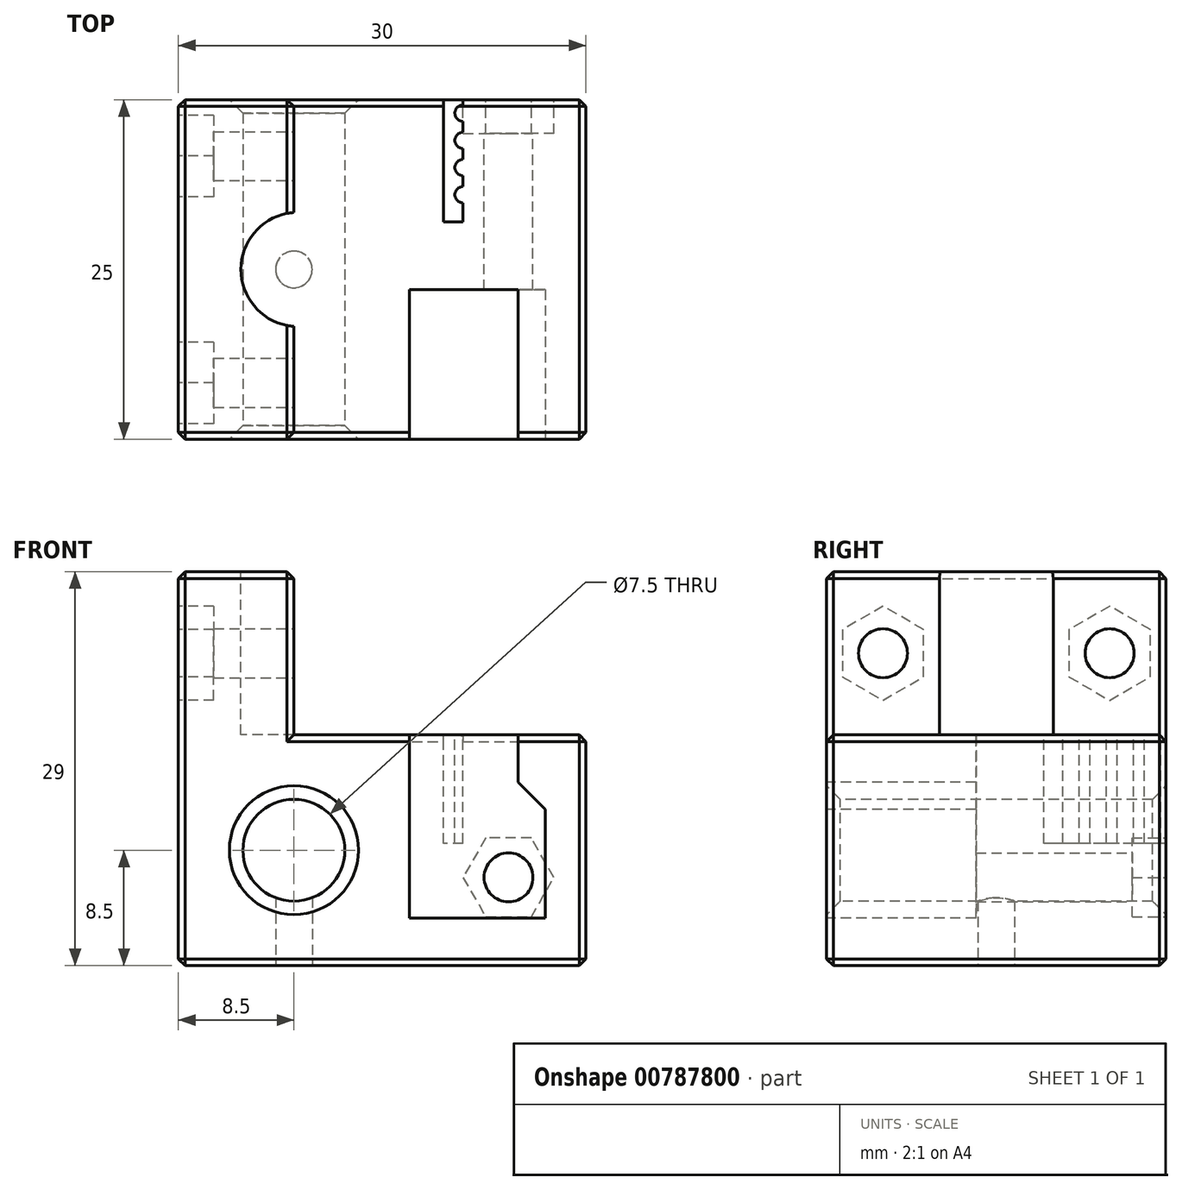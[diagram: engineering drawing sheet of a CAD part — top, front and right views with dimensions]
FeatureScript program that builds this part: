
annotation { "Feature Type Name" : "Feature", "Feature Type Description" : "" }
export const myFeature = defineFeature(function(context is Context, id is Id, definition is map)
    precondition{}
    {
        {
            var Q0;
            Q0=qCreatedBy(makeId("Top.planeOp"),FACE);
            var sketch = newSketch(context, id + "F0", { "sketchPlane" : qUnion([Q0])});
            skLineSegment(sketch, "E0.bottom", {"start": v(15, 12.5) * mm, "end": v(-15, 12.5) * mm});
            skLineSegment(sketch, "E0.top", {"start": v(15, -12.5) * mm, "end": v(-15, -12.5) * mm});
            skLineSegment(sketch, "E0.left", {"start": v(15, 12.5) * mm, "end": v(15, -12.5) * mm});
            skLineSegment(sketch, "E0.right", {"start": v(-15, 12.5) * mm, "end": v(-15, -12.5) * mm});
            skPoint(sketch, "E0.middle", {"position": v(0, 0) * mm});
            skSolve(sketch);
        }
        {
            var Q0;
            Q0=makeQuery(id+"F0.imprint","IMPRINT",FACE,{"disambiguationData":[TD([[makeQuery(id+"F0.imprint","IMPRINT",EDGE,{"derivedFrom":sQuery(id+"F0.wireOp",EDGE,"E0.bottom")}),1.0]])]});
            extrude(context, id + "F1", {"entities" : qUnion([Q0]), "depth" : 17 * mm, "offsetDistance" : 25 * mm});
        }
        {
            var Q0;
            Q0=makeQuery(id+"F1.opExtrude","SWEPT_FACE",FACE,{"disambiguationData":[OSD([sQuery(id+"F0.wireOp",EDGE,"E0.top")])]});
            var sketch = newSketch(context, id + "F2", { "sketchPlane" : qUnion([Q0])});
            skLineSegment(sketch, "E1", {"start": v(2, 17) * mm, "end": v(10, 17) * mm});
            skLineSegment(sketch, "E2", {"start": v(10, 17) * mm, "end": v(10, 13.5) * mm});
            skLineSegment(sketch, "E3", {"start": v(10, 13.5) * mm, "end": v(12, 11.5) * mm});
            skLineSegment(sketch, "E4", {"start": v(12, 11.5) * mm, "end": v(12, 3.5) * mm});
            skLineSegment(sketch, "E5", {"start": v(12, 3.5) * mm, "end": v(2, 3.5) * mm});
            skLineSegment(sketch, "E6", {"start": v(2, 3.5) * mm, "end": v(2, 17) * mm});
            skSolve(sketch);
        }
        {
            var Q0;
            Q0=makeQuery(id+"F2.imprint","IMPRINT",FACE,{"disambiguationData":[TD([[makeQuery(id+"F2.imprint","IMPRINT",EDGE,{"derivedFrom":sQuery(id+"F2.wireOp",EDGE,"E1")}),1.0]])]});
            extrude(context, id + "F3", {"entities" : qUnion([Q0]), "operationType" : NewBodyOperationType.REMOVE, "oppositeDirection" : true, "depth" : 11 * mm, "offsetDistance" : 25 * mm});
        }
        {
            var Q0;
            Q0=makeQuery(id+"F1.opExtrude","SWEPT_FACE",FACE,{"disambiguationData":[OSD([sQuery(id+"F0.wireOp",EDGE,"E0.top")])]});
            var sketch = newSketch(context, id + "F4", { "sketchPlane" : qUnion([Q0])});
            skCircle(sketch, "E7", {"center": v(-6.5, 8.5) * mm, "radius": 3.75 * mm});
            skPoint(sketch, "E7.centerSnap0", {"position": v(-6.5, 17) * mm});
            skPoint(sketch, "E7.centerSnap1", {"position": v(-15, 8.5) * mm});
            skSolve(sketch);
        }
        {
            var Q0;
            Q0=makeQuery(id+"F4.imprint","IMPRINT",FACE,{"disambiguationData":[TD([[makeQuery(id+"F4.imprint","IMPRINT",EDGE,{"derivedFrom":sQuery(id+"F4.wireOp",EDGE,"E7")}),1.0]])]});
            extrude(context, id + "F5", {"entities" : qUnion([Q0]), "operationType" : NewBodyOperationType.REMOVE, "endBound" : BoundingType.UP_TO_NEXT, "oppositeDirection" : true, "depth" : 25 * mm, "offsetDistance" : 25 * mm});
        }
        {
            var Q0;
            Q0=makeQuery(id+"F1.opExtrude","CAP_FACE",FACE,{"disambiguationData":[OSD([sQuery(id+"F0.wireOp",EDGE,"E0.bottom"),sQuery(id+"F0.wireOp",EDGE,"E0.top"),sQuery(id+"F0.wireOp",EDGE,"E0.left"),sQuery(id+"F0.wireOp",EDGE,"E0.right")])],"isStart":false});
            var sketch = newSketch(context, id + "F6", { "sketchPlane" : qUnion([Q0])});
            skLineSegment(sketch, "E8.bottom", {"start": v(-6.5, -12.5) * mm, "end": v(-15, -12.5) * mm});
            skLineSegment(sketch, "E8.top", {"start": v(-6.5, 12.5) * mm, "end": v(-15, 12.5) * mm});
            skLineSegment(sketch, "E8.left", {"start": v(-6.5, -12.5) * mm, "end": v(-6.5, 12.5) * mm});
            skLineSegment(sketch, "E8.right", {"start": v(-15, -12.5) * mm, "end": v(-15, 12.5) * mm});
            skSolve(sketch);
        }
        {
            var Q0;
            {var subQ1=sQuery(id+"F6.wireOp",EDGE,"E8.bottom");Q0=makeQuery(id+"F6.imprint","IMPRINT",FACE,{"disambiguationData":[TD([[makeQuery(id+"F6.imprint","IMPRINT",EDGE,{"derivedFrom":subQ1}),-1.0]])]});}
            extrude(context, id + "F7", {"entities" : qUnion([Q0]), "operationType" : NewBodyOperationType.ADD, "depth" : 12 * mm, "offsetDistance" : 25 * mm});
        }
        {
            var Q0;
            Q0=makeQuery(id+"F7.opExtrude","CAP_FACE",FACE,{"disambiguationData":[OSD([sQuery(id+"F6.wireOp",EDGE,"E8.bottom"),sQuery(id+"F6.wireOp",EDGE,"E8.top"),sQuery(id+"F6.wireOp",EDGE,"E8.left"),sQuery(id+"F6.wireOp",EDGE,"E8.right")])],"isStart":false});
            var sketch = newSketch(context, id + "F8", { "sketchPlane" : qUnion([Q0])});
            skArc(sketch, "E9", {"start": v(-6.5, 4.19) * mm, "mid": v(-10.4, 0) * mm, "end": v(-6.5, -4.19) * mm});
            skLineSegment(sketch, "E10", {"start": v(-6.5, -4.19) * mm, "end": v(-6.5, 4.19) * mm});
            skSolve(sketch);
        }
        {
            var Q0;
            Q0=makeQuery(id+"F8.imprint","IMPRINT",FACE,{"disambiguationData":[TD([[makeQuery(id+"F8.imprint","IMPRINT",EDGE,{"derivedFrom":sQuery(id+"F8.wireOp",EDGE,"E9")}),1.0]])]});
            extrude(context, id + "F9", {"entities" : qUnion([Q0]), "operationType" : NewBodyOperationType.REMOVE, "oppositeDirection" : true, "depth" : 12 * mm, "offsetDistance" : 25 * mm});
        }
        {
            var Q0;
            {var subQ0=sQuery(id+"F6.wireOp",EDGE,"E8.left");var subQ2=sQuery(id+"F0.wireOp",EDGE,"E0.bottom");Q0=makeQuery(id+"F9.boolean.opBoolean","SPLIT",FACE,{"disambiguationData":[TD([makeQuery(id+"F1.opExtrude","SWEPT_FACE",FACE,{"disambiguationData":[OSD([subQ2])]})])],"derivedFrom":makeQuery(id+"F7.opExtrude","SWEPT_FACE",FACE,{"disambiguationData":[OSD([subQ0])]})});}
            var sketch = newSketch(context, id + "F10", { "sketchPlane" : qUnion([Q0])});
            skPoint(sketch, "E11.centerSnap0", {"position": v(-12.5, 14.5) * mm});
            skPoint(sketch, "E11.centerSnap1", {"position": v(0, 29) * mm});
            skCircle(sketch, "E12", {"center": v(8.34, 23) * mm, "radius": 1.8 * mm});
            skPoint(sketch, "E12.centerSnap0", {"position": v(12.5, 23) * mm});
            skPoint(sketch, "E12.centerSnap1", {"position": v(8.34, 29) * mm});
            skPoint(sketch, "E13.0", {"position": v(-8.34, 29) * mm});
            skCircle(sketch, "E14", {"center": v(-8.34, 23) * mm, "radius": 1.8 * mm});
            skPoint(sketch, "E14.centerSnap0", {"position": v(4.19, 23) * mm});
            skSolve(sketch);
        }
        {
            var Q0;
            Q0=makeQuery(id+"F10.imprint","IMPRINT",FACE,{"disambiguationData":[TD([[makeQuery(id+"F10.imprint","IMPRINT",EDGE,{"derivedFrom":sQuery(id+"F10.wireOp",EDGE,"E14")}),1.0]])]});
            var Q1;
            Q1=makeQuery(id+"F10.imprint","IMPRINT",FACE,{"disambiguationData":[TD([[makeQuery(id+"F10.imprint","IMPRINT",EDGE,{"derivedFrom":sQuery(id+"F10.wireOp",EDGE,"E12")}),1.0]])]});
            extrude(context, id + "F11", {"entities" : qUnion([Q0, Q1]), "operationType" : NewBodyOperationType.REMOVE, "endBound" : BoundingType.UP_TO_NEXT, "oppositeDirection" : true, "depth" : 25 * mm, "offsetDistance" : 25 * mm});
        }
        {
            var Q0;
            Q0=makeQuery(id+"F7.boolean.opBoolean","MERGE",FACE,{"derivedFrom":[makeQuery(id+"F1.opExtrude","SWEPT_FACE",FACE,{"disambiguationData":[OSD([sQuery(id+"F0.wireOp",EDGE,"E0.right")])]}),makeQuery(id+"F7.opExtrude","SWEPT_FACE",FACE,{"disambiguationData":[OSD([sQuery(id+"F6.wireOp",EDGE,"E8.right")])]})]});
            var sketch = newSketch(context, id + "F12", { "sketchPlane" : qUnion([Q0])});
            skCircle(sketch, "E15.cCircle", {"center": v(8.34, 23) * mm, "radius": 3 * mm, "construction": true});
            skLineSegment(sketch, "E15.0", {"start": v(11.34, 24.73) * mm, "end": v(11.34, 21.27) * mm});
            skLineSegment(sketch, "E15.1", {"start": v(11.34, 21.27) * mm, "end": v(8.34, 19.54) * mm});
            skLineSegment(sketch, "E15.2", {"start": v(8.34, 19.54) * mm, "end": v(5.34, 21.27) * mm});
            skLineSegment(sketch, "E15.3", {"start": v(5.34, 21.27) * mm, "end": v(5.34, 24.73) * mm});
            skLineSegment(sketch, "E15.4", {"start": v(5.34, 24.73) * mm, "end": v(8.34, 26.46) * mm});
            skLineSegment(sketch, "E15.5", {"start": v(8.34, 26.46) * mm, "end": v(11.34, 24.73) * mm});
            skPoint(sketch, "E15.0.midPoint", {"position": v(11.34, 23) * mm});
            skCircle(sketch, "E16.cCircle", {"center": v(-8.34, 23) * mm, "radius": 3 * mm, "construction": true});
            skLineSegment(sketch, "E16.0", {"start": v(-5.34, 24.73) * mm, "end": v(-5.34, 21.27) * mm});
            skLineSegment(sketch, "E16.1", {"start": v(-5.34, 21.27) * mm, "end": v(-8.34, 19.54) * mm});
            skLineSegment(sketch, "E16.2", {"start": v(-8.34, 19.54) * mm, "end": v(-11.34, 21.27) * mm});
            skLineSegment(sketch, "E16.3", {"start": v(-11.34, 21.27) * mm, "end": v(-11.34, 24.73) * mm});
            skLineSegment(sketch, "E16.4", {"start": v(-11.34, 24.73) * mm, "end": v(-8.34, 26.46) * mm});
            skLineSegment(sketch, "E16.5", {"start": v(-8.34, 26.46) * mm, "end": v(-5.34, 24.73) * mm});
            skPoint(sketch, "E16.0.midPoint", {"position": v(-5.34, 23) * mm});
            skSolve(sketch);
        }
        {
            var Q0;
            Q0=makeQuery(id+"F12.imprint","IMPRINT",FACE,{"disambiguationData":[TD([[makeQuery(id+"F12.imprint","IMPRINT",EDGE,{"derivedFrom":sQuery(id+"F12.wireOp",EDGE,"E15.0")}),-1.0]])]});
            var Q1;
            Q1=makeQuery(id+"F12.imprint","IMPRINT",FACE,{"disambiguationData":[TD([[makeQuery(id+"F12.imprint","IMPRINT",EDGE,{"derivedFrom":sQuery(id+"F12.wireOp",EDGE,"E16.0")}),-1.0]])]});
            extrude(context, id + "F13", {"entities" : qUnion([Q0, Q1]), "operationType" : NewBodyOperationType.REMOVE, "oppositeDirection" : true, "depth" : 2.6 * mm, "offsetDistance" : 25 * mm});
        }
        {
            var Q0;
            {var subQ0=sQuery(id+"F0.wireOp",EDGE,"E0.left");var subQ1=sQuery(id+"F0.wireOp",EDGE,"E0.top");var subQ4=sQuery(id+"F0.wireOp",EDGE,"E0.bottom");Q0=makeQuery(id+"F7.boolean.opBoolean","SPLIT",FACE,{"disambiguationData":[TD([makeQuery(id+"F1.opExtrude","SWEPT_FACE",FACE,{"disambiguationData":[OSD([subQ0])]})])],"derivedFrom":makeQuery(id+"F1.opExtrude","CAP_FACE",FACE,{"disambiguationData":[OSD([subQ4,subQ1,subQ0,sQuery(id+"F0.wireOp",EDGE,"E0.right")])],"isStart":false})});}
            var sketch = newSketch(context, id + "F14", { "sketchPlane" : qUnion([Q0])});
            skLineSegment(sketch, "E17.bottom", {"start": v(4.5, 12.5) * mm, "end": v(5.95, 12.5) * mm});
            skLineSegment(sketch, "E17.top", {"start": v(4.5, 3.5) * mm, "end": v(5.95, 3.5) * mm});
            skLineSegment(sketch, "E17.left", {"start": v(4.5, 12.5) * mm, "end": v(4.5, 3.5) * mm});
            skLineSegment(sketch, "E17.right", {"start": v(5.95, 12.5) * mm, "end": v(5.95, 12.1) * mm});
            skArc(sketch, "E18", {"start": v(5.95, 12.1) * mm, "mid": v(5.35, 11.5) * mm, "end": v(5.95, 10.9) * mm});
            skArc(sketch, "E19.0.1.0", {"start": v(5.95, 10.1) * mm, "mid": v(5.35, 9.5) * mm, "end": v(5.95, 8.9) * mm});
            skArc(sketch, "E19.0.2.0", {"start": v(5.95, 8.1) * mm, "mid": v(5.35, 7.5) * mm, "end": v(5.95, 6.9) * mm});
            skArc(sketch, "E19.0.3.0", {"start": v(5.95, 6.1) * mm, "mid": v(5.35, 5.5) * mm, "end": v(5.95, 4.9) * mm});
            skLineSegment(sketch, "E19.direction1", {"start": v(5.95, 11.5) * mm, "end": v(13.56, 11.5) * mm, "construction": true});
            skLineSegment(sketch, "E19.direction2", {"start": v(5.95, 11.5) * mm, "end": v(5.95, 9.5) * mm, "construction": true});
            skLineSegment(sketch, "E20.trimOffspring", {"start": v(5.95, 4.9) * mm, "end": v(5.95, 3.5) * mm});
            skLineSegment(sketch, "E21.trimOffspring", {"start": v(5.95, 6.9) * mm, "end": v(5.95, 6.1) * mm});
            skLineSegment(sketch, "E22.trimOffspring", {"start": v(5.95, 8.9) * mm, "end": v(5.95, 8.1) * mm});
            skLineSegment(sketch, "E23.trimOffspring", {"start": v(5.95, 11.5) * mm, "end": v(5.95, 9.5) * mm});
            skSolve(sketch);
        }
        {
            var Q0;
            Q0=makeQuery(id+"F14.imprint","IMPRINT",FACE,{"disambiguationData":[TD([[makeQuery(id+"F14.imprint","IMPRINT",EDGE,{"derivedFrom":sQuery(id+"F14.wireOp",EDGE,"E17.bottom")}),1.0]])]});
            extrude(context, id + "F15", {"entities" : qUnion([Q0]), "operationType" : NewBodyOperationType.REMOVE, "oppositeDirection" : true, "depth" : 8 * mm, "offsetDistance" : 25 * mm});
        }
        {
            var Q0;
            Q0=makeQuery(id+"F7.boolean.opBoolean","MERGE",FACE,{"derivedFrom":[makeQuery(id+"F1.opExtrude","SWEPT_FACE",FACE,{"disambiguationData":[OSD([sQuery(id+"F0.wireOp",EDGE,"E0.bottom")])]}),makeQuery(id+"F7.opExtrude","SWEPT_FACE",FACE,{"disambiguationData":[OSD([sQuery(id+"F6.wireOp",EDGE,"E8.top")])]})]});
            var sketch = newSketch(context, id + "F16", { "sketchPlane" : qUnion([Q0])});
            skCircle(sketch, "E24", {"center": v(-9.3, 6.5) * mm, "radius": 1.8 * mm});
            skSolve(sketch);
        }
        {
            var Q0;
            Q0=makeQuery(id+"F16.imprint","IMPRINT",FACE,{"disambiguationData":[TD([[makeQuery(id+"F16.imprint","IMPRINT",EDGE,{"derivedFrom":sQuery(id+"F16.wireOp",EDGE,"E24")}),1.0]])]});
            extrude(context, id + "F17", {"entities" : qUnion([Q0]), "operationType" : NewBodyOperationType.REMOVE, "endBound" : BoundingType.UP_TO_NEXT, "oppositeDirection" : true, "depth" : 25 * mm, "offsetDistance" : 25 * mm});
        }
        {
            var Q0;
            Q0=makeQuery(id+"F7.boolean.opBoolean","MERGE",FACE,{"derivedFrom":[makeQuery(id+"F1.opExtrude","SWEPT_FACE",FACE,{"disambiguationData":[OSD([sQuery(id+"F0.wireOp",EDGE,"E0.bottom")])]}),makeQuery(id+"F7.opExtrude","SWEPT_FACE",FACE,{"disambiguationData":[OSD([sQuery(id+"F6.wireOp",EDGE,"E8.top")])]})]});
            var sketch = newSketch(context, id + "F18", { "sketchPlane" : qUnion([Q0])});
            skCircle(sketch, "E25.cCircle", {"center": v(-9.3, 6.5) * mm, "radius": 2.9 * mm, "construction": true});
            skLineSegment(sketch, "E25.0", {"start": v(-10.97, 9.4) * mm, "end": v(-7.63, 9.4) * mm});
            skLineSegment(sketch, "E25.1", {"start": v(-7.63, 9.4) * mm, "end": v(-5.95, 6.5) * mm});
            skLineSegment(sketch, "E25.2", {"start": v(-5.95, 6.5) * mm, "end": v(-7.63, 3.6) * mm});
            skLineSegment(sketch, "E25.3", {"start": v(-7.63, 3.6) * mm, "end": v(-10.97, 3.6) * mm});
            skLineSegment(sketch, "E25.4", {"start": v(-10.97, 3.6) * mm, "end": v(-12.65, 6.5) * mm});
            skLineSegment(sketch, "E25.5", {"start": v(-12.65, 6.5) * mm, "end": v(-10.97, 9.4) * mm});
            skPoint(sketch, "E25.0.midPoint", {"position": v(-9.3, 9.4) * mm});
            skSolve(sketch);
        }
        {
            var Q0;
            Q0=makeQuery(id+"F18.imprint","IMPRINT",FACE,{"disambiguationData":[TD([[makeQuery(id+"F18.imprint","IMPRINT",EDGE,{"derivedFrom":sQuery(id+"F18.wireOp",EDGE,"E25.0")}),-1.0]])]});
            extrude(context, id + "F19", {"entities" : qUnion([Q0]), "operationType" : NewBodyOperationType.REMOVE, "oppositeDirection" : true, "depth" : 2.5 * mm, "offsetDistance" : 25 * mm});
        }
        {
            var Q0;
            Q0=makeQuery(id+"F7.boolean.opBoolean","MERGE",FACE,{"derivedFrom":[makeQuery(id+"F1.opExtrude","SWEPT_FACE",FACE,{"disambiguationData":[OSD([sQuery(id+"F0.wireOp",EDGE,"E0.bottom")])]}),makeQuery(id+"F7.opExtrude","SWEPT_FACE",FACE,{"disambiguationData":[OSD([sQuery(id+"F6.wireOp",EDGE,"E8.top")])]})]});
            var sketch = newSketch(context, id + "F20", { "sketchPlane" : qUnion([Q0])});
            skCircle(sketch, "E26.0", {"center": v(6.5, 8.5) * mm, "radius": 3.75 * mm});
            skCircle(sketch, "E27", {"center": v(6.5, 8.5) * mm, "radius": 3.5 * mm});
            skLineSegment(sketch, "E28", {"start": v(5.35, 11.8) * mm, "end": v(5.29, 12.05) * mm});
            skLineSegment(sketch, "E29", {"start": v(7.65, 11.8) * mm, "end": v(7.71, 12.05) * mm});
            skLineSegment(sketch, "E30", {"start": v(6.5, -1.55) * mm, "end": v(6.5, 19.4) * mm});
            skLineSegment(sketch, "E31.1.0", {"start": v(8.79, 11.15) * mm, "end": v(8.97, 11.33) * mm});
            skLineSegment(sketch, "E31.1.1", {"start": v(9.94, 9.16) * mm, "end": v(10.18, 9.22) * mm});
            skLineSegment(sketch, "E31.2.0", {"start": v(9.94, 7.84) * mm, "end": v(10.18, 7.78) * mm});
            skLineSegment(sketch, "E31.2.1", {"start": v(8.79, 5.85) * mm, "end": v(8.97, 5.67) * mm});
            skLineSegment(sketch, "E31.3.0", {"start": v(7.65, 5.2) * mm, "end": v(7.71, 4.95) * mm});
            skLineSegment(sketch, "E31.3.1", {"start": v(5.35, 5.2) * mm, "end": v(5.29, 4.95) * mm});
            skLineSegment(sketch, "E31.4.0", {"start": v(4.21, 5.85) * mm, "end": v(4.03, 5.67) * mm});
            skLineSegment(sketch, "E31.4.1", {"start": v(3.06, 7.84) * mm, "end": v(2.82, 7.78) * mm});
            skLineSegment(sketch, "E31.5.0", {"start": v(3.06, 9.16) * mm, "end": v(2.82, 9.22) * mm});
            skLineSegment(sketch, "E31.5.1", {"start": v(4.21, 11.15) * mm, "end": v(4.03, 11.33) * mm});
            skLineSegment(sketch, "E31.anchor1", {"start": v(6.5, 8.5) * mm, "end": v(5.35, 11.8) * mm, "construction": true});
            skLineSegment(sketch, "E31.anchor2", {"start": v(6.5, 8.5) * mm, "end": v(5.35, 11.8) * mm, "construction": true});
            skSolve(sketch);
        }
        {
            var Q0;
            Q0=makeQuery(id+"F1.opExtrude","CAP_EDGE",EDGE,{"disambiguationData":[OSD([sQuery(id+"F0.wireOp",EDGE,"E0.top")])],"isStart":true});
            var Q1;
            Q1=makeQuery(id+"F1.opExtrude","CAP_EDGE",EDGE,{"disambiguationData":[OSD([sQuery(id+"F0.wireOp",EDGE,"E0.right")])],"isStart":true});
            var Q2;
            Q2=makeQuery(id+"F1.opExtrude","CAP_EDGE",EDGE,{"disambiguationData":[OSD([sQuery(id+"F0.wireOp",EDGE,"E0.bottom")])],"isStart":true});
            var Q3;
            Q3=makeQuery(id+"F1.opExtrude","CAP_EDGE",EDGE,{"disambiguationData":[OSD([sQuery(id+"F0.wireOp",EDGE,"E0.left")])],"isStart":true});
            var Q4;
            Q4=makeQuery(id+"F1.opExtrude","CAP_EDGE",EDGE,{"disambiguationData":[OSD([sQuery(id+"F0.wireOp",EDGE,"E0.right")])],"isStart":false});
            var Q5;
            {var subQ0=sQuery(id+"F0.wireOp",EDGE,"E0.right");var subQ1=sQuery(id+"F0.wireOp",EDGE,"E0.bottom");Q5=makeQuery(id+"F7.boolean.opBoolean","SPLIT",EDGE,{"disambiguationData":[TD([makeQuery(id+"F1.opExtrude","SWEPT_FACE",FACE,{"disambiguationData":[OSD([subQ0])]})])],"derivedFrom":makeQuery(id+"F1.opExtrude","CAP_EDGE",EDGE,{"disambiguationData":[OSD([subQ1])],"isStart":false})});}
            var Q6;
            Q6=makeQuery(id+"F1.opExtrude","SWEPT_EDGE",EDGE,{"disambiguationData":[OSD([sQuery(id+"F0.wireOp",EDGE,"E0.bottom"),sQuery(id+"F0.wireOp",EDGE,"E0.right")])]});
            var Q7;
            Q7=makeQuery(id+"F1.opExtrude","SWEPT_EDGE",EDGE,{"disambiguationData":[OSD([sQuery(id+"F0.wireOp",EDGE,"E0.top"),sQuery(id+"F0.wireOp",EDGE,"E0.right")])]});
            var Q8;
            Q8=makeQuery(id+"F7.boolean.opBoolean","MERGE",EDGE,{"derivedFrom":[makeQuery(id+"F3.boolean.opBoolean","COPY",EDGE,{"derivedFrom":makeQuery(id+"F3.opExtrude","CAP_EDGE",EDGE,{"disambiguationData":[OSD([sQuery(id+"F2.wireOp",EDGE,"E6")])],"isStart":true})}),makeQuery(id+"F7.opExtrude","SWEPT_EDGE",EDGE,{"disambiguationData":[OSD([sQuery(id+"F6.wireOp",EDGE,"E8.bottom"),sQuery(id+"F6.wireOp",EDGE,"E8.left")])]})]});
            var Q9;
            Q9=makeQuery(id+"F3.boolean.opBoolean","COPY",EDGE,{"derivedFrom":makeQuery(id+"F3.opExtrude","CAP_EDGE",EDGE,{"disambiguationData":[OSD([sQuery(id+"F2.wireOp",EDGE,"E5")])],"isStart":true})});
            var Q10;
            Q10=makeQuery(id+"F3.boolean.opBoolean","COPY",EDGE,{"derivedFrom":makeQuery(id+"F3.opExtrude","CAP_EDGE",EDGE,{"disambiguationData":[OSD([sQuery(id+"F2.wireOp",EDGE,"E4")])],"isStart":true})});
            var Q11;
            Q11=makeQuery(id+"F3.boolean.opBoolean","COPY",EDGE,{"derivedFrom":makeQuery(id+"F3.opExtrude","CAP_EDGE",EDGE,{"disambiguationData":[OSD([sQuery(id+"F2.wireOp",EDGE,"E3")])],"isStart":true})});
            var Q12;
            Q12=makeQuery(id+"F3.boolean.opBoolean","COPY",EDGE,{"derivedFrom":makeQuery(id+"F3.opExtrude","CAP_EDGE",EDGE,{"disambiguationData":[OSD([sQuery(id+"F2.wireOp",EDGE,"E2")])],"isStart":true})});
            var Q13;
            Q13=makeQuery(id+"F1.opExtrude","SWEPT_EDGE",EDGE,{"disambiguationData":[OSD([sQuery(id+"F0.wireOp",EDGE,"E0.top"),sQuery(id+"F0.wireOp",EDGE,"E0.left")])]});
            var Q14;
            {var subQ0=sQuery(id+"F0.wireOp",EDGE,"E0.left");var subQ1=sQuery(id+"F0.wireOp",EDGE,"E0.top");Q14=makeQuery(id+"F3.boolean.opBoolean","SPLIT",EDGE,{"disambiguationData":[TD([makeQuery(id+"F1.opExtrude","SWEPT_FACE",FACE,{"disambiguationData":[OSD([subQ0])]})])],"derivedFrom":makeQuery(id+"F1.opExtrude","CAP_EDGE",EDGE,{"disambiguationData":[OSD([subQ1])],"isStart":false})});}
            var Q15;
            Q15=makeQuery(id+"F1.opExtrude","CAP_EDGE",EDGE,{"disambiguationData":[OSD([sQuery(id+"F0.wireOp",EDGE,"E0.left")])],"isStart":false});
            var Q16;
            Q16=makeQuery(id+"F1.opExtrude","SWEPT_EDGE",EDGE,{"disambiguationData":[OSD([sQuery(id+"F0.wireOp",EDGE,"E0.bottom"),sQuery(id+"F0.wireOp",EDGE,"E0.left")])]});
            var Q17;
            {var subQ0=sQuery(id+"F0.wireOp",EDGE,"E0.left");var subQ1=makeQuery(id+"F1.opExtrude","SWEPT_FACE",FACE,{"disambiguationData":[OSD([subQ0])]});var subQ2=sQuery(id+"F0.wireOp",EDGE,"E0.bottom");Q17=makeQuery(id+"F15.boolean.opBoolean","SPLIT",EDGE,{"disambiguationData":[TD([subQ1])],"derivedFrom":makeQuery(id+"F7.boolean.opBoolean","SPLIT",EDGE,{"disambiguationData":[TD([subQ1])],"derivedFrom":makeQuery(id+"F1.opExtrude","CAP_EDGE",EDGE,{"disambiguationData":[OSD([subQ2])],"isStart":false})})});}
            var Q18;
            {var subQ0=sQuery(id+"F0.wireOp",EDGE,"E0.left");var subQ1=sQuery(id+"F0.wireOp",EDGE,"E0.bottom");var subQ4=makeQuery(id+"F3.boolean.opBoolean","COPY",FACE,{"derivedFrom":makeQuery(id+"F3.opExtrude","SWEPT_FACE",FACE,{"disambiguationData":[OSD([sQuery(id+"F2.wireOp",EDGE,"E6")])]})});Q18=makeQuery(id+"F15.boolean.opBoolean","SPLIT",EDGE,{"disambiguationData":[TD([subQ4])],"derivedFrom":makeQuery(id+"F7.boolean.opBoolean","SPLIT",EDGE,{"disambiguationData":[TD([makeQuery(id+"F1.opExtrude","SWEPT_FACE",FACE,{"disambiguationData":[OSD([subQ0])]})])],"derivedFrom":makeQuery(id+"F1.opExtrude","CAP_EDGE",EDGE,{"disambiguationData":[OSD([subQ1])],"isStart":false})})});}
            var Q19;
            Q19=makeQuery(id+"F7.opExtrude","SWEPT_EDGE",EDGE,{"disambiguationData":[OSD([sQuery(id+"F0.wireOp",EDGE,"E0.bottom"),sQuery(id+"F6.wireOp",EDGE,"E8.top"),sQuery(id+"F6.wireOp",EDGE,"E8.left")])]});
            var Q20;
            Q20=makeQuery(id+"F7.opExtrude","SWEPT_EDGE",EDGE,{"disambiguationData":[OSD([sQuery(id+"F0.wireOp",EDGE,"E0.bottom"),sQuery(id+"F6.wireOp",EDGE,"E8.top"),sQuery(id+"F6.wireOp",EDGE,"E8.right")])]});
            var Q21;
            Q21=makeQuery(id+"F7.opExtrude","CAP_EDGE",EDGE,{"disambiguationData":[OSD([sQuery(id+"F6.wireOp",EDGE,"E8.top")])],"isStart":false});
            var Q22;
            Q22=makeQuery(id+"F7.opExtrude","CAP_EDGE",EDGE,{"disambiguationData":[OSD([sQuery(id+"F6.wireOp",EDGE,"E8.left")])],"isStart":false});
            var Q23;
            Q23=makeQuery(id+"F7.opExtrude","CAP_EDGE",EDGE,{"disambiguationData":[OSD([sQuery(id+"F6.wireOp",EDGE,"E8.bottom")])],"isStart":false});
            var Q24;
            {var subQ0=sQuery(id+"F0.wireOp",EDGE,"E0.right");var subQ1=sQuery(id+"F0.wireOp",EDGE,"E0.top");Q24=makeQuery(id+"F3.boolean.opBoolean","SPLIT",EDGE,{"disambiguationData":[TD([makeQuery(id+"F1.opExtrude","SWEPT_FACE",FACE,{"disambiguationData":[OSD([subQ0])]})])],"derivedFrom":makeQuery(id+"F1.opExtrude","CAP_EDGE",EDGE,{"disambiguationData":[OSD([subQ1])],"isStart":false})});}
            var Q25;
            {var subQ0=sQuery(id+"F6.wireOp",EDGE,"E8.right");Q25=makeQuery(id+"F9.boolean.opBoolean","SPLIT",EDGE,{"disambiguationData":[TD([makeQuery(id+"F1.opExtrude","SWEPT_FACE",FACE,{"disambiguationData":[OSD([sQuery(id+"F0.wireOp",EDGE,"E0.top")])]})])],"derivedFrom":makeQuery(id+"F7.opExtrude","CAP_EDGE",EDGE,{"disambiguationData":[OSD([subQ0])],"isStart":false})});}
            var Q26;
            Q26=makeQuery(id+"F9.boolean.opBoolean","COPY",EDGE,{"derivedFrom":makeQuery(id+"F9.opExtrude","CAP_EDGE",EDGE,{"disambiguationData":[OSD([sQuery(id+"F8.wireOp",EDGE,"QR7yRkyR-xB5Y-inZ7-O5XR-Qu2GMxaPGScG")])],"isStart":true})});
            var Q27;
            {var subQ0=sQuery(id+"F6.wireOp",EDGE,"E8.right");Q27=makeQuery(id+"F9.boolean.opBoolean","SPLIT",EDGE,{"disambiguationData":[TD([makeQuery(id+"F1.opExtrude","SWEPT_FACE",FACE,{"disambiguationData":[OSD([sQuery(id+"F0.wireOp",EDGE,"E0.bottom")])]})])],"derivedFrom":makeQuery(id+"F7.opExtrude","CAP_EDGE",EDGE,{"disambiguationData":[OSD([subQ0])],"isStart":false})});}
            var Q28;
            Q28=makeQuery(id+"F7.opExtrude","SWEPT_EDGE",EDGE,{"disambiguationData":[OSD([sQuery(id+"F0.wireOp",EDGE,"E0.top"),sQuery(id+"F6.wireOp",EDGE,"E8.bottom"),sQuery(id+"F6.wireOp",EDGE,"E8.left")])]});
            var Q29;
            Q29=makeQuery(id+"F9.boolean.opBoolean","COPY",EDGE,{"derivedFrom":makeQuery(id+"F9.opExtrude","CAP_EDGE",EDGE,{"disambiguationData":[OSD([sQuery(id+"F8.wireOp",EDGE,"E9")])],"isStart":true})});
            var Q30;
            Q30=makeQuery(id+"F3.boolean.opBoolean","COPY",EDGE,{"derivedFrom":makeQuery(id+"F3.opExtrude","CAP_EDGE",EDGE,{"disambiguationData":[OSD([sQuery(id+"F2.wireOp",EDGE,"E6")])],"isStart":true})});
            chamfer(context, id + "F21", {"entities" : qUnion([Q0, Q1, Q2, Q3, Q4, Q5, Q6, Q7, Q8, Q9, Q10, Q11, Q12, Q13, Q14, Q15, Q16, Q17, Q18, Q19, Q20, Q21, Q22, Q23, Q24, Q25, Q26, Q27, Q28, Q29, Q30]), "width" : 0.5 * mm, "tangentPropagation" : true});
        }
        {
            var Q0;
            Q0=makeQuery(id+"F5.boolean.opBoolean","COPY",FACE,{"derivedFrom":makeQuery(id+"F5.opExtrude","SWEPT_FACE",FACE,{"disambiguationData":[OSD([sQuery(id+"F4.wireOp",EDGE,"E7")])]})});
            chamfer(context, id + "F22", {"entities" : qUnion([Q0]), "chamferType" : ChamferType.OFFSET_ANGLE, "width" : 1 * mm, "oppositeDirection" : false, "angle" : 45 * degree, "tangentPropagation" : true});
        }
        {
            var Q0;
            Q0=makeQuery(id+"F1.opExtrude","CAP_FACE",FACE,{"disambiguationData":[OSD([sQuery(id+"F0.wireOp",EDGE,"E0.bottom"),sQuery(id+"F0.wireOp",EDGE,"E0.top"),sQuery(id+"F0.wireOp",EDGE,"E0.left"),sQuery(id+"F0.wireOp",EDGE,"E0.right")])],"isStart":true});
            var sketch = newSketch(context, id + "F23", { "sketchPlane" : qUnion([Q0])});
            skPoint(sketch, "E32.0", {"position": v(-6.5, -12.5) * mm});
            skCircle(sketch, "E33", {"center": v(-6.5, 0) * mm, "radius": 1.35 * mm});
            skPoint(sketch, "E33.centerSnap0", {"position": v(-14.5, 0) * mm});
            skSolve(sketch);
        }
        {
            var Q0;
            Q0=makeQuery(id+"F23.imprint","IMPRINT",FACE,{"disambiguationData":[TD([[makeQuery(id+"F23.imprint","IMPRINT",EDGE,{"derivedFrom":sQuery(id+"F23.wireOp",EDGE,"E33")}),1.0]])]});
            extrude(context, id + "F24", {"entities" : qUnion([Q0]), "operationType" : NewBodyOperationType.REMOVE, "endBound" : BoundingType.UP_TO_NEXT, "oppositeDirection" : true, "depth" : 25 * mm, "offsetDistance" : 25 * mm});
        }
    });
